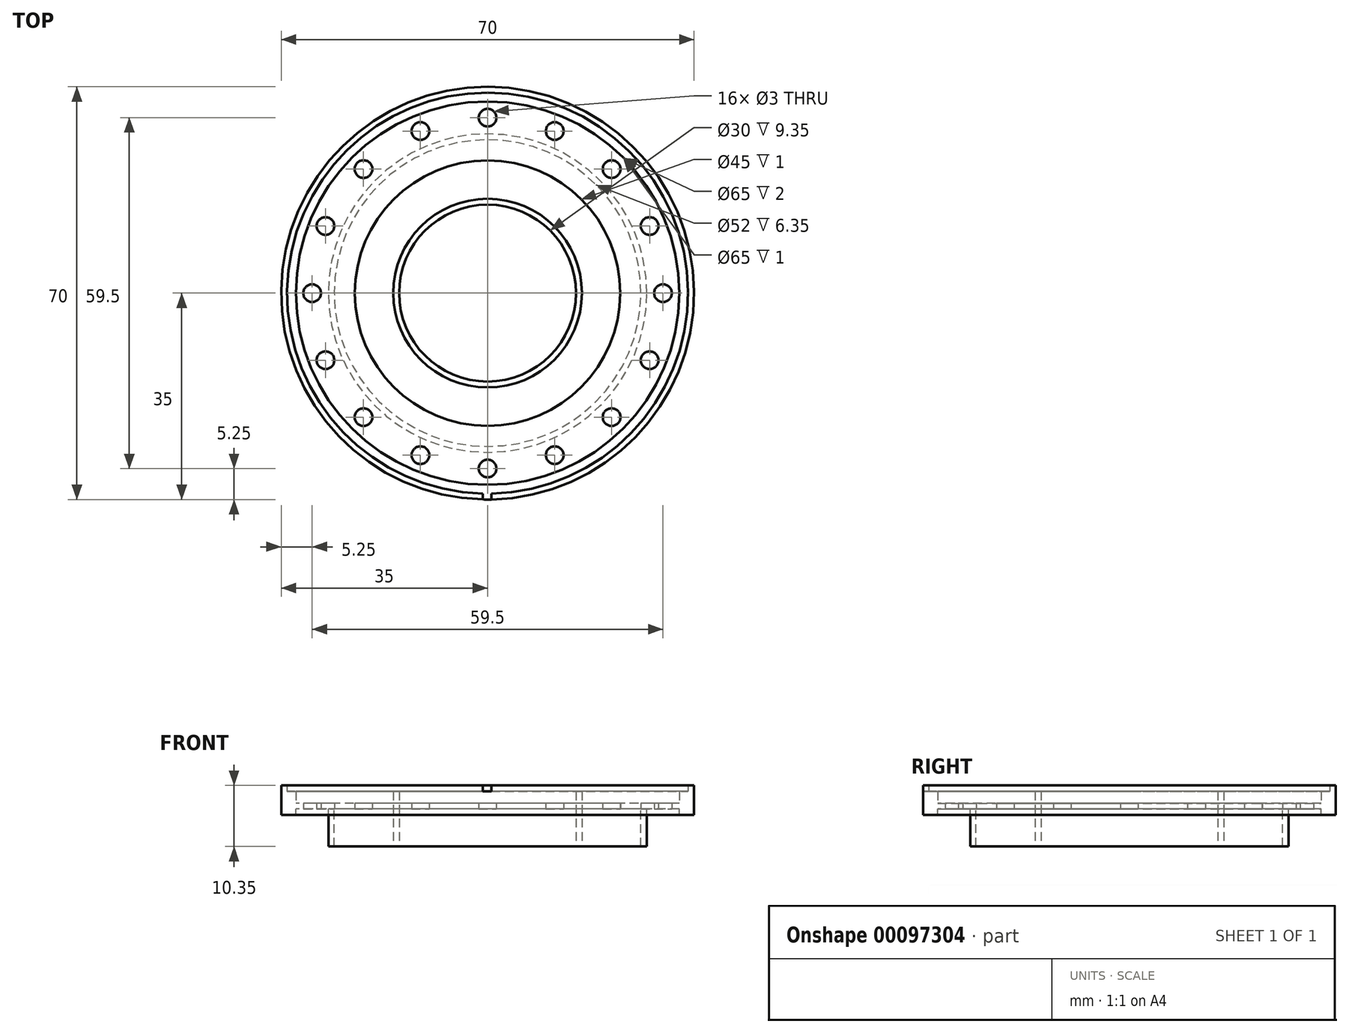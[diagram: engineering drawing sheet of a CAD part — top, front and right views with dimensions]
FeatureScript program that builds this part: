
annotation { "Feature Type Name" : "Feature", "Feature Type Description" : "" }
export const myFeature = defineFeature(function(context is Context, id is Id, definition is map)
    precondition{}
    {
        {
            var Q0;
            Q0=qCreatedBy(makeId("Top.planeOp"),FACE);
            var sketch = newSketch(context, id + "F0", { "sketchPlane" : qUnion([Q0])});
            skPoint(sketch, "E0", {"position": v(-22.5, 0) * mm});
            skPoint(sketch, "E1", {"position": v(-32.5, 0) * mm});
            skPoint(sketch, "E2", {"position": v(-34, 0) * mm});
            skPoint(sketch, "E3", {"position": v(-35, 0) * mm});
            skCircle(sketch, "E4", {"center": v(0, 0) * mm, "radius": 22.5 * mm});
            skCircle(sketch, "E5", {"center": v(0, 0) * mm, "radius": 32.5 * mm});
            skCircle(sketch, "E6", {"center": v(0, 0) * mm, "radius": 35 * mm});
            skPoint(sketch, "E7", {"position": v(15, 0) * mm});
            skPoint(sketch, "E8", {"position": v(16, 0) * mm});
            skCircle(sketch, "E9", {"center": v(0, 0) * mm, "radius": 15 * mm});
            skCircle(sketch, "E10", {"center": v(0, 0) * mm, "radius": 16 * mm});
            skLineSegment(sketch, "E11", {"start": v(-0.82, -35.7) * mm, "end": v(-0.82, -35) * mm});
            skLineSegment(sketch, "E12", {"start": v(0.64, -32.37) * mm, "end": v(0.64, -32.5) * mm});
            skArc(sketch, "E13", {"start": v(0.64, -34) * mm, "mid": v(0.1, 34) * mm, "end": v(-0.82, -34) * mm});
            skLineSegment(sketch, "E14", {"start": v(0.64, -35) * mm, "end": v(0.64, -35.7) * mm});
            skLineSegment(sketch, "E15", {"start": v(-0.82, -35) * mm, "end": v(-0.82, -32.49) * mm});
            skLineSegment(sketch, "E16", {"start": v(-0.82, -32.49) * mm, "end": v(-0.82, -32.37) * mm});
            skLineSegment(sketch, "E17", {"start": v(0.64, -32.5) * mm, "end": v(0.64, -35) * mm});
            skSolve(sketch);
        }
        {
            var Q0;
            Q0=makeQuery(id+"F0.imprint","IMPRINT",FACE,{"disambiguationData":[TD([[makeQuery(id+"F0.imprint","IMPRINT",EDGE,{"derivedFrom":sQuery(id+"F0.wireOp",EDGE,"E4")}),-1.0]])]});
            extrude(context, id + "F1", {"entities" : qUnion([Q0]), "depth" : 1 * mm});
        }
        {
            var Q0;
            {var subQ5=sQuery(id+"F0.wireOp",EDGE,"E13");Q0=makeQuery(id+"F0.imprint","IMPRINT",FACE,{"disambiguationData":[TD([[makeQuery(id+"F0.imprint","IMPRINT",EDGE,{"derivedFrom":subQ5}),1.0]])]});}
            var Q1;
            {var subQ3=sQuery(id+"F0.wireOp",EDGE,"E5");var subQ7=sQuery(id+"F0.wireOp",EDGE,"E17");var subQ8=makeQuery(id+"F0.imprint","INTERSECT",VERTEX,{"derivedFrom":[subQ3,subQ7]});Q1=makeQuery(id+"F0.imprint","IMPRINT",FACE,{"disambiguationData":[TD([[makeQuery(id+"F0.imprint","IMPRINT",EDGE,{"disambiguationData":[TD([[subQ8,1.0]])],"derivedFrom":subQ3}),-1.0]])]});}
            extrude(context, id + "F2", {"entities" : qUnion([Q0, Q1]), "operationType" : NewBodyOperationType.ADD, "depth" : 3 * mm});
        }
        {
            var Q0;
            {var subQ5=sQuery(id+"F0.wireOp",EDGE,"E13");Q0=makeQuery(id+"F0.imprint","IMPRINT",FACE,{"disambiguationData":[TD([[makeQuery(id+"F0.imprint","IMPRINT",EDGE,{"derivedFrom":subQ5}),-1.0]])]});}
            extrude(context, id + "F3", {"entities" : qUnion([Q0]), "operationType" : NewBodyOperationType.ADD, "depth" : 4 * mm});
        }
        {
            var Q0;
            Q0=makeQuery(id+"F0.imprint","IMPRINT",FACE,{"disambiguationData":[TD([[makeQuery(id+"F0.imprint","IMPRINT",EDGE,{"derivedFrom":sQuery(id+"F0.wireOp",EDGE,"E4")}),-1.0]])]});
            var sketch = newSketch(context, id + "F4", { "sketchPlane" : qUnion([Q0])});
            skPoint(sketch, "E18", {"position": v(-27, 0) * mm});
            skPoint(sketch, "E19", {"position": v(-26, 0) * mm});
            skCircle(sketch, "E20", {"center": v(0, 0) * mm, "radius": 26 * mm});
            skCircle(sketch, "E21", {"center": v(0, 0) * mm, "radius": 27 * mm});
            skPoint(sketch, "E22", {"position": v(-32.5, 0) * mm});
            skPoint(sketch, "E23", {"position": v(-35, 0) * mm});
            skCircle(sketch, "E24", {"center": v(0, 0) * mm, "radius": 32.5 * mm});
            skCircle(sketch, "E25", {"center": v(0, 0) * mm, "radius": 35 * mm});
            skLineSegment(sketch, "E26", {"start": v(-32.5, 0) * mm, "end": v(-27, 0) * mm});
            skPoint(sketch, "E27", {"position": v(-29.75, 0) * mm});
            skCircle(sketch, "E28", {"center": v(-29.75, 0) * mm, "radius": 1.5 * mm});
            skCircle(sketch, "E29.1.0", {"center": v(-27.49, 11.38) * mm, "radius": 1.5 * mm});
            skCircle(sketch, "E29.2.0", {"center": v(-21.04, 21.04) * mm, "radius": 1.5 * mm});
            skCircle(sketch, "E29.3.0", {"center": v(-11.38, 27.49) * mm, "radius": 1.5 * mm});
            skCircle(sketch, "E29.4.0", {"center": v(0, 29.75) * mm, "radius": 1.5 * mm});
            skCircle(sketch, "E29.5.0", {"center": v(11.38, 27.49) * mm, "radius": 1.5 * mm});
            skCircle(sketch, "E29.6.0", {"center": v(21.04, 21.04) * mm, "radius": 1.5 * mm});
            skCircle(sketch, "E29.7.0", {"center": v(27.49, 11.38) * mm, "radius": 1.5 * mm});
            skCircle(sketch, "E29.8.0", {"center": v(29.75, 0) * mm, "radius": 1.5 * mm});
            skCircle(sketch, "E29.9.0", {"center": v(27.49, -11.38) * mm, "radius": 1.5 * mm});
            skCircle(sketch, "E29.10.0", {"center": v(21.04, -21.04) * mm, "radius": 1.5 * mm});
            skCircle(sketch, "E29.11.0", {"center": v(11.38, -27.49) * mm, "radius": 1.5 * mm});
            skCircle(sketch, "E29.12.0", {"center": v(0, -29.75) * mm, "radius": 1.5 * mm});
            skCircle(sketch, "E29.13.0", {"center": v(-11.38, -27.49) * mm, "radius": 1.5 * mm});
            skCircle(sketch, "E29.14.0", {"center": v(-21.04, -21.04) * mm, "radius": 1.5 * mm});
            skCircle(sketch, "E29.15.0", {"center": v(-27.49, -11.38) * mm, "radius": 1.5 * mm});
            skLineSegment(sketch, "E29.anchor1", {"start": v(0, 0) * mm, "end": v(-29.75, 0) * mm, "construction": true});
            skLineSegment(sketch, "E29.anchor2", {"start": v(0, 0) * mm, "end": v(-27.49, -11.38) * mm, "construction": true});
            skSolve(sketch);
        }
        {
            var Q0;
            Q0=makeQuery(id+"F4.imprint","IMPRINT",FACE,{"disambiguationData":[TD([[makeQuery(id+"F4.imprint","IMPRINT",EDGE,{"derivedFrom":sQuery(id+"F4.wireOp",EDGE,"E20")}),-1.0]])]});
            extrude(context, id + "F5", {"entities" : qUnion([Q0]), "operationType" : NewBodyOperationType.ADD, "oppositeDirection" : true, "depth" : 6.35 * mm});
        }
        {
            var Q0;
            Q0=sQuery(id+"F4.wireOp",VERTEX,"E29.13.0.center");
            var Q1;
            Q1=sQuery(id+"F4.wireOp",VERTEX,"E29.12.0.center");
            var Q2;
            Q2=sQuery(id+"F4.wireOp",VERTEX,"E29.11.0.center");
            var Q3;
            Q3=sQuery(id+"F4.wireOp",VERTEX,"E29.10.0.center");
            var Q4;
            Q4=sQuery(id+"F4.wireOp",VERTEX,"E29.9.0.center");
            var Q5;
            Q5=sQuery(id+"F4.wireOp",VERTEX,"E29.8.0.center");
            var Q6;
            Q6=sQuery(id+"F4.wireOp",VERTEX,"E29.7.0.center");
            var Q7;
            Q7=sQuery(id+"F4.wireOp",VERTEX,"E29.6.0.center");
            var Q8;
            Q8=sQuery(id+"F4.wireOp",VERTEX,"E29.5.0.center");
            var Q9;
            Q9=sQuery(id+"F4.wireOp",VERTEX,"E29.4.0.center");
            var Q10;
            Q10=sQuery(id+"F4.wireOp",VERTEX,"E29.3.0.center");
            var Q11;
            Q11=sQuery(id+"F4.wireOp",VERTEX,"E29.2.0.center");
            var Q12;
            Q12=sQuery(id+"F4.wireOp",VERTEX,"E29.1.0.center");
            var Q13;
            Q13=sQuery(id+"F4.wireOp",VERTEX,"E27");
            var Q14;
            Q14=sQuery(id+"F4.wireOp",VERTEX,"E29.anchor2.end");
            var Q15;
            Q15=sQuery(id+"F4.wireOp",VERTEX,"E29.14.0.center");
            var Q16;
            Q16=makeQuery(id+"F1.opExtrude","SWEPT_BODY",BODY,{"disambiguationData":[OSD([sQuery(id+"F0.wireOp",EDGE,"E4"),sQuery(id+"F0.wireOp",EDGE,"E5")])]});
            hole(context, id + "F6", {"style" : HoleStyle.SIMPLE, "endStyle" : HoleEndStyle.THROUGH, "oppositeDirection" : true, "holeDiameter" : 3 * mm, "locations" : qUnion([Q0, Q1, Q2, Q3, Q4, Q5, Q6, Q7, Q8, Q9, Q10, Q11, Q12, Q13, Q14, Q15]), "scope" : qUnion([Q16]), "isTappedThrough" : true});
        }
        {
            var Q0;
            Q0=makeQuery(id+"F0.imprint","IMPRINT",FACE,{"disambiguationData":[TD([[makeQuery(id+"F0.imprint","IMPRINT",EDGE,{"derivedFrom":sQuery(id+"F0.wireOp",EDGE,"E9")}),-1.0]])]});
            var Q1;
            Q1=makeQuery(id+"F2.opExtrude","CAP_FACE",FACE,{"disambiguationData":[OSD([sQuery(id+"F0.wireOp",EDGE,"E5"),sQuery(id+"F0.wireOp",EDGE,"yBU4XXtD-m5E6-ZDvU-JST3-c3MBXM4o9OfY")])],"isStart":false});
            var Q2;
            Q2=makeQuery(id+"F5.opExtrude","CAP_FACE",FACE,{"disambiguationData":[OSD([sQuery(id+"F4.wireOp",EDGE,"E20"),sQuery(id+"F4.wireOp",EDGE,"E21")])],"isStart":false});
            extrude(context, id + "F7", {"entities" : qUnion([Q0]), "endBound" : BoundingType.UP_TO_SURFACE, "endBoundEntityFace" : qUnion([Q1]), "depth" : 25.4 * mm, "hasSecondDirection" : true, "secondDirectionBound" : SecondDirectionBoundingType.UP_TO_SURFACE, "secondDirectionOppositeDirection" : true, "secondDirectionBoundEntityFace" : qUnion([Q2]), "secondDirectionDepth" : 25.4 * mm});
        }
        {
            var Q0;
            Q0=makeQuery(id+"F4.imprint","IMPRINT",FACE,{"disambiguationData":[TD([[makeQuery(id+"F4.imprint","IMPRINT",EDGE,{"derivedFrom":sQuery(id+"F4.wireOp",EDGE,"E24")}),-1.0]])]});
            extrude(context, id + "F8", {"entities" : qUnion([Q0]), "operationType" : NewBodyOperationType.ADD, "oppositeDirection" : true, "depth" : 1 * mm});
        }
    });
